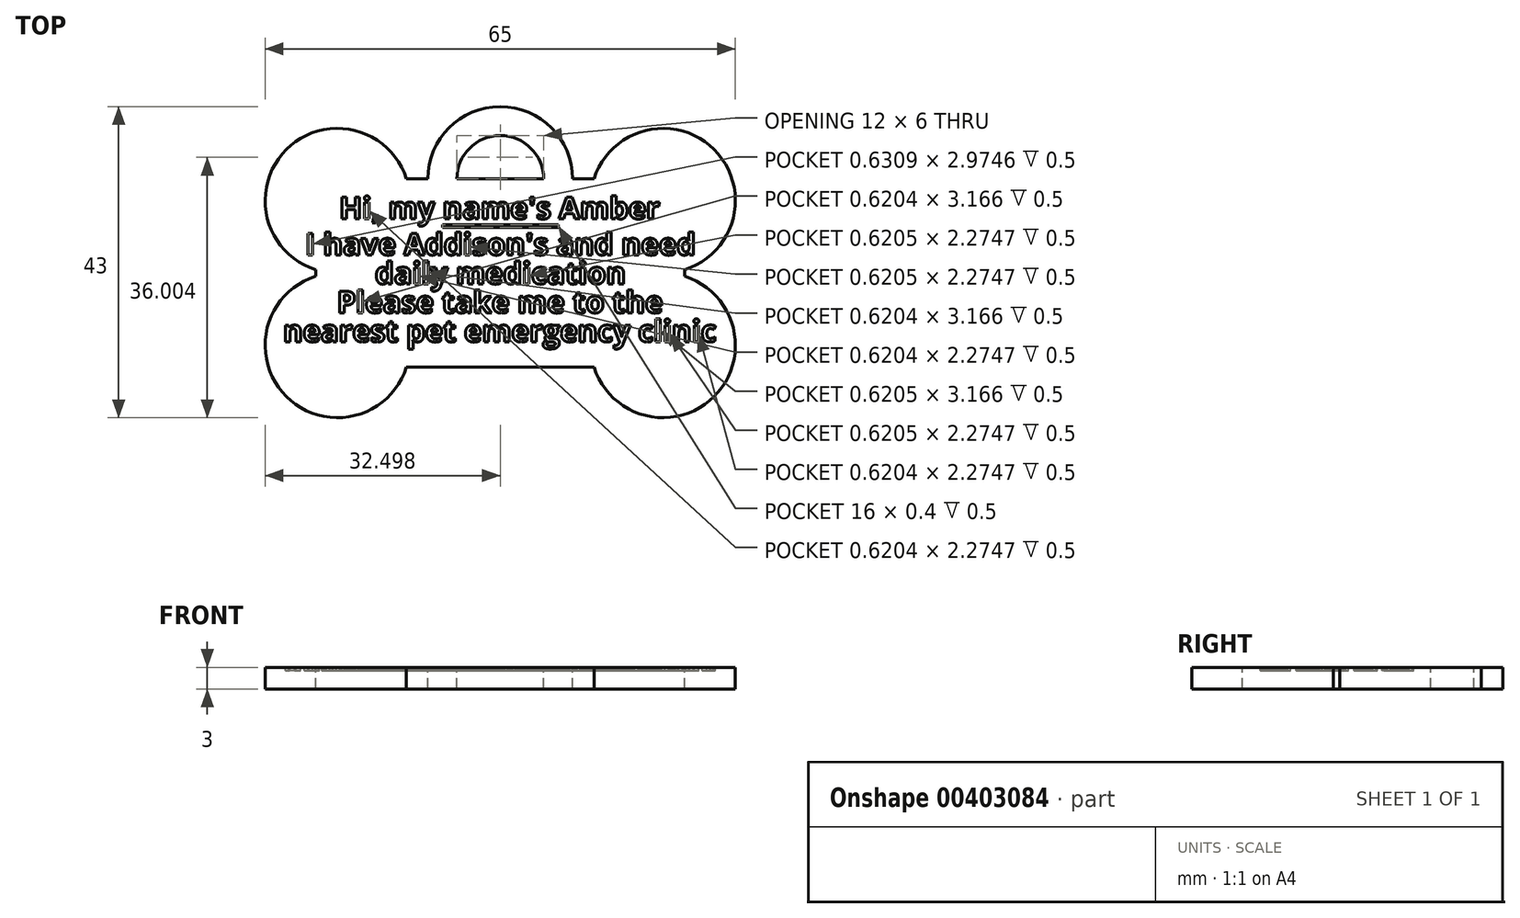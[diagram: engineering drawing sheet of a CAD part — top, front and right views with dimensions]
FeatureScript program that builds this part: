
annotation { "Feature Type Name" : "Feature", "Feature Type Description" : "" }
export const myFeature = defineFeature(function(context is Context, id is Id, definition is map)
    precondition{}
    {
        {
            var Q0;
            Q0=qCreatedBy(makeId("Top.planeOp"),FACE);
            var sketch = newSketch(context, id + "F0", { "sketchPlane" : qUnion([Q0])});
            skLineSegment(sketch, "E0.bottom", {"start": v(-16.01, 14.85) * mm, "end": v(28.99, 14.85) * mm});
            skLineSegment(sketch, "E0.top", {"start": v(-16.01, -5.15) * mm, "end": v(28.99, -5.15) * mm});
            skLineSegment(sketch, "E0.left", {"start": v(-16.01, 14.85) * mm, "end": v(-16.01, -5.15) * mm});
            skLineSegment(sketch, "E0.right", {"start": v(28.99, 14.85) * mm, "end": v(28.99, -5.15) * mm});
            skSolve(sketch);
        }
        {
            var Q0;
            Q0 = qSketchRegion(id + "F0", true);
            extrude(context, id + "F1", {"entities" : qUnion([Q0]), "depth" : 3 * mm});
        }
        {
            var Q0;
            Q0=makeQuery(id+"F1.opExtrude","CAP_FACE",FACE,{"disambiguationData":[OSD([sQuery(id+"F0.wireOp",EDGE,"E0.bottom"),sQuery(id+"F0.wireOp",EDGE,"E0.top"),sQuery(id+"F0.wireOp",EDGE,"E0.left"),sQuery(id+"F0.wireOp",EDGE,"E0.right")])],"isStart":false});
            var sketch = newSketch(context, id + "F2", { "sketchPlane" : qUnion([Q0])});
            skCircle(sketch, "E1", {"center": v(28.99, 14.85) * mm, "radius": 10 * mm});
            skCircle(sketch, "E2", {"center": v(28.99, -5.15) * mm, "radius": 10 * mm});
            skCircle(sketch, "E3", {"center": v(-16.01, -5.15) * mm, "radius": 10 * mm});
            skCircle(sketch, "E4", {"center": v(-16.01, 14.85) * mm, "radius": 10 * mm});
            skSolve(sketch);
        }
        {
            var Q0;
            Q0 = qSketchRegion(id + "F2", true);
            extrude(context, id + "F3", {"entities" : qUnion([Q0]), "operationType" : NewBodyOperationType.ADD, "oppositeDirection" : true, "depth" : 3 * mm});
        }
        {
            var Q0;
            Q0=makeQuery(id+"F3.boolean.opBoolean","MERGE",FACE,{"derivedFrom":[makeQuery(id+"F1.opExtrude","CAP_FACE",FACE,{"disambiguationData":[OSD([sQuery(id+"F0.wireOp",EDGE,"E0.bottom"),sQuery(id+"F0.wireOp",EDGE,"E0.top"),sQuery(id+"F0.wireOp",EDGE,"E0.left"),sQuery(id+"F0.wireOp",EDGE,"E0.right")])],"isStart":false}),makeQuery(id+"F3.opExtrude","CAP_FACE",FACE,{"disambiguationData":[OSD([sQuery(id+"F2.wireOp",EDGE,"E1")])],"isStart":true}),makeQuery(id+"F3.opExtrude","CAP_FACE",FACE,{"disambiguationData":[OSD([sQuery(id+"F2.wireOp",EDGE,"E2")])],"isStart":true}),makeQuery(id+"F3.opExtrude","CAP_FACE",FACE,{"disambiguationData":[OSD([sQuery(id+"F2.wireOp",EDGE,"E3")])],"isStart":true}),makeQuery(id+"F3.opExtrude","CAP_FACE",FACE,{"disambiguationData":[OSD([sQuery(id+"F2.wireOp",EDGE,"E4")])],"isStart":true})]});
            var sketch = newSketch(context, id + "F4", { "sketchPlane" : qUnion([Q0])});
            skLineSegment(sketch, "E5.bottom", {"start": v(-19.01, 17.85) * mm, "end": v(31.99, 17.85) * mm});
            skLineSegment(sketch, "E5.top", {"start": v(-19.01, -8.15) * mm, "end": v(31.99, -8.15) * mm});
            skLineSegment(sketch, "E5.left", {"start": v(-19.01, 17.85) * mm, "end": v(-19.01, -8.15) * mm});
            skLineSegment(sketch, "E5.right", {"start": v(31.99, 17.85) * mm, "end": v(31.99, -8.15) * mm});
            skSolve(sketch);
        }
        {
            var Q0;
            Q0 = qSketchRegion(id + "F4", true);
            extrude(context, id + "F5", {"entities" : qUnion([Q0]), "operationType" : NewBodyOperationType.ADD, "oppositeDirection" : true, "depth" : 3 * mm});
        }
        {
            var Q0;
            {var subQ5=makeQuery(id+"F1.opExtrude","CAP_EDGE",EDGE,{"disambiguationData":[OSD([sQuery(id+"F0.wireOp",EDGE,"E0.bottom")])],"isStart":false});Q0=makeQuery(id+"F4.imprint","IMPRINT",FACE,{"disambiguationData":[TD([[makeQuery(id+"F4.imprint","IMPRINT",EDGE,{"derivedFrom":subQ5}),1.0]])]});}
            var sketch = newSketch(context, id + "F6", { "sketchPlane" : qUnion([Q0])});
            skCircle(sketch, "E6", {"center": v(6.49, 17.85) * mm, "radius": 10 * mm});
            skCircle(sketch, "E7", {"center": v(6.49, 17.85) * mm, "radius": 6 * mm});
            skSolve(sketch);
        }
        {
            var Q0;
            Q0 = qSketchRegion(id + "F6", true);
            var Q1;
            Q1 = qConstructionFilter(qBodyType(qCreatedBy(id + "F6" ,EDGE), BodyType.WIRE), ConstructionObject.NO);
            extrude(context, id + "F7", {"entities" : qUnion([Q0]), "operationType" : NewBodyOperationType.ADD, "surfaceEntities" : qUnion([Q1]), "oppositeDirection" : true, "depth" : 3 * mm});
        }
        {
            var Q0;
            Q0=makeQuery(id+"F5.boolean.opBoolean","MERGE",FACE,{"derivedFrom":[makeQuery(id+"F3.boolean.opBoolean","MERGE",FACE,{"derivedFrom":[makeQuery(id+"F1.opExtrude","CAP_FACE",FACE,{"disambiguationData":[OSD([sQuery(id+"F0.wireOp",EDGE,"E0.bottom"),sQuery(id+"F0.wireOp",EDGE,"E0.top"),sQuery(id+"F0.wireOp",EDGE,"E0.left"),sQuery(id+"F0.wireOp",EDGE,"E0.right")])],"isStart":false}),makeQuery(id+"F3.opExtrude","CAP_FACE",FACE,{"disambiguationData":[OSD([sQuery(id+"F2.wireOp",EDGE,"E1")])],"isStart":true}),makeQuery(id+"F3.opExtrude","CAP_FACE",FACE,{"disambiguationData":[OSD([sQuery(id+"F2.wireOp",EDGE,"E2")])],"isStart":true}),makeQuery(id+"F3.opExtrude","CAP_FACE",FACE,{"disambiguationData":[OSD([sQuery(id+"F2.wireOp",EDGE,"E3")])],"isStart":true}),makeQuery(id+"F3.opExtrude","CAP_FACE",FACE,{"disambiguationData":[OSD([sQuery(id+"F2.wireOp",EDGE,"E4")])],"isStart":true})]}),makeQuery(id+"F5.opExtrude","CAP_FACE",FACE,{"disambiguationData":[OSD([sQuery(id+"F4.wireOp",EDGE,"E5.bottom"),sQuery(id+"F4.wireOp",EDGE,"E5.top"),sQuery(id+"F4.wireOp",EDGE,"E5.left"),sQuery(id+"F4.wireOp",EDGE,"E5.right")])],"isStart":true})]});
            var sketch = newSketch(context, id + "F8", { "sketchPlane" : qUnion([Q0])});
            skText(sketch, "E8", { "text": "I have Addison\'s and need", "fontName": "OpenSans-Bold.ttf"});
            skText(sketch, "E9", { "text": "daily medication", "fontName": "OpenSans-Bold.ttf"});
            skText(sketch, "E10", { "text": "Please take me to the", "fontName": "OpenSans-Bold.ttf"});
            skPoint(sketch, "E10.firstSnap0", {"position": v(-10.82, 4.85) * mm});
            skText(sketch, "E11", { "text": "nearest pet emergency clinic", "fontName": "OpenSans-Bold.ttf"});
            skLineSegment(sketch, "E12", {"start": v(6.49, 17.85) * mm, "end": v(6.49, -8.15) * mm, "construction": true});
            skText(sketch, "E13", { "text": "Hi, my name\'s Amber", "fontName": "OpenSans-Bold.ttf"});
            skLineSegment(sketch, "E14.bottom", {"start": v(-1.51, 11.55) * mm, "end": v(14.49, 11.55) * mm});
            skLineSegment(sketch, "E14.top", {"start": v(-1.51, 11.15) * mm, "end": v(14.49, 11.15) * mm});
            skLineSegment(sketch, "E14.left", {"start": v(-1.51, 11.55) * mm, "end": v(-1.51, 11.15) * mm});
            skLineSegment(sketch, "E14.right", {"start": v(14.49, 11.55) * mm, "end": v(14.49, 11.15) * mm});
            const initialGuessF8  = {"E8": [-0.02047, 0.00735, 1, 0, 0.003], "E9": [-0.01082, 0.00335, 1, 0, 0.003], "E10": [-0.01608, -0.00065, 1, 0, 0.003], "E11": [-0.02354, -0.00465, 1, 0, 0.003], "E13": [-0.01576, 0.01235, 1, 0, 0.003]};
            skSetInitialGuess(sketch, initialGuessF8);
            skSolve(sketch);
        }
        {
            var Q0;
            Q0 = qSketchRegion(id + "F8", true);
            extrude(context, id + "F9", {"entities" : qUnion([Q0]), "operationType" : NewBodyOperationType.REMOVE, "oppositeDirection" : true, "depth" : .5 * mm});
        }
    });
